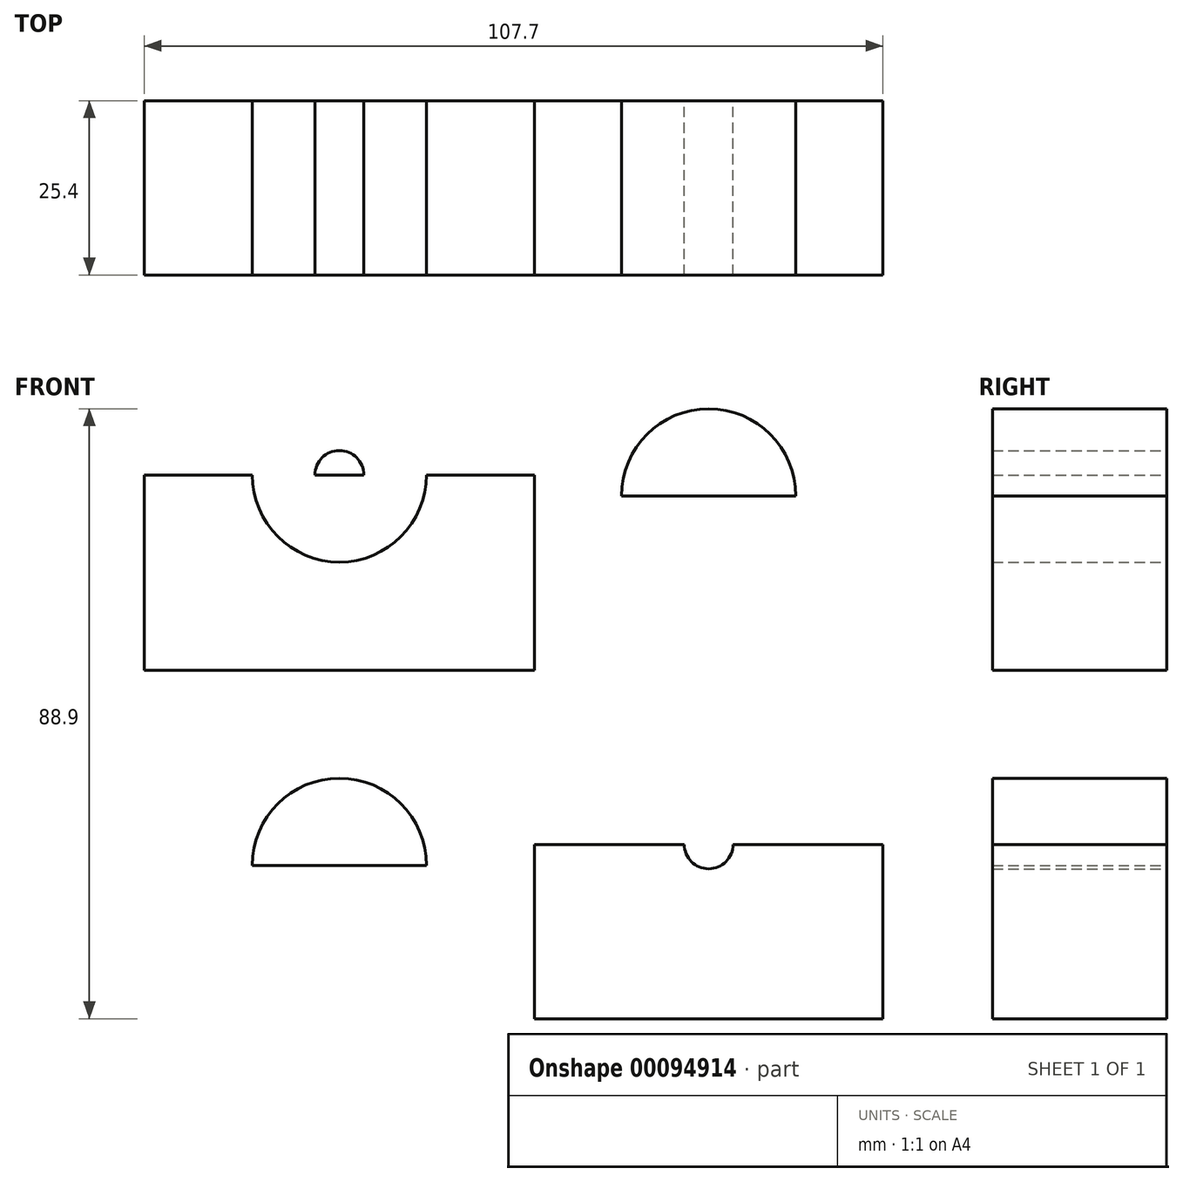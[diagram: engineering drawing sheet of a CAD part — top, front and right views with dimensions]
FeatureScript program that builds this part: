
annotation { "Feature Type Name" : "Feature", "Feature Type Description" : "" }
export const myFeature = defineFeature(function(context is Context, id is Id, definition is map)
    precondition{}
    {
        {
            var Q0;
            Q0=qCreatedBy(makeId("Front.planeOp"),FACE);
            var sketch = newSketch(context, id + "F0", { "sketchPlane" : qUnion([Q0])});
            skLineSegment(sketch, "E0", {"start": v(0, 0) * mm, "end": v(50.8, 0) * mm});
            skLineSegment(sketch, "E1", {"start": v(50.8, 0) * mm, "end": v(50.8, 50.8) * mm});
            skLineSegment(sketch, "E2", {"start": v(50.8, 50.8) * mm, "end": v(0, 50.8) * mm});
            skLineSegment(sketch, "E3", {"start": v(0, 50.8) * mm, "end": v(0, 0) * mm});
            skLineSegment(sketch, "E4", {"start": v(25.4, 50.8) * mm, "end": v(25.4, 0) * mm});
            skLineSegment(sketch, "E5", {"start": v(0, 25.4) * mm, "end": v(50.8, 25.4) * mm});
            skCircle(sketch, "E6", {"center": v(25.4, 25.4) * mm, "radius": 12.7 * mm});
            skCircle(sketch, "E7", {"center": v(25.4, 25.4) * mm, "radius": 3.56 * mm});
            skSolve(sketch);
        }
        {
            var Q0;
            {var subQ0=sQuery(id+"F0.wireOp",EDGE,"E6");var subQ1=sQuery(id+"F0.wireOp",EDGE,"E4");var subQ2=makeQuery(id+"F0.imprint","INTERSECT",VERTEX,{"disambiguationData":[OD(0.0)],"derivedFrom":[subQ1,subQ0]});Q0=makeQuery(id+"F0.imprint","IMPRINT",FACE,{"disambiguationData":[TD([[makeQuery(id+"F0.imprint","IMPRINT",EDGE,{"disambiguationData":[TD([[subQ2,-1.0]])],"derivedFrom":subQ1}),1.0]])]});}
            var Q1;
            {var subQ0=sQuery(id+"F0.wireOp",EDGE,"E6");var subQ1=sQuery(id+"F0.wireOp",EDGE,"E4");var subQ2=makeQuery(id+"F0.imprint","INTERSECT",VERTEX,{"disambiguationData":[OD(0.0)],"derivedFrom":[subQ1,subQ0]});Q1=makeQuery(id+"F0.imprint","IMPRINT",FACE,{"disambiguationData":[TD([[makeQuery(id+"F0.imprint","IMPRINT",EDGE,{"disambiguationData":[TD([[subQ2,-1.0]])],"derivedFrom":subQ1}),-1.0]])]});}
            var Q2;
            {var subQ0=sQuery(id+"F0.wireOp",EDGE,"E7");var subQ1=sQuery(id+"F0.wireOp",EDGE,"E4");var subQ2=makeQuery(id+"F0.imprint","INTERSECT",VERTEX,{"disambiguationData":[OD(1.0)],"derivedFrom":[subQ1,subQ0]});Q2=makeQuery(id+"F0.imprint","IMPRINT",FACE,{"disambiguationData":[TD([[makeQuery(id+"F0.imprint","IMPRINT",EDGE,{"disambiguationData":[TD([[subQ2,-1.0]])],"derivedFrom":subQ1}),-1.0]])]});}
            var Q3;
            {var subQ0=sQuery(id+"F0.wireOp",EDGE,"E7");var subQ1=sQuery(id+"F0.wireOp",EDGE,"E4");var subQ2=makeQuery(id+"F0.imprint","INTERSECT",VERTEX,{"disambiguationData":[OD(1.0)],"derivedFrom":[subQ1,subQ0]});Q3=makeQuery(id+"F0.imprint","IMPRINT",FACE,{"disambiguationData":[TD([[makeQuery(id+"F0.imprint","IMPRINT",EDGE,{"disambiguationData":[TD([[subQ2,-1.0]])],"derivedFrom":subQ1}),1.0]])]});}
            extrude(context, id + "F1", {"entities" : qUnion([Q0, Q1, Q2, Q3]), "depth" : 25.4 * mm});
        }
        {
            var Q0;
            Q0=qCreatedBy(makeId("Front.planeOp"),FACE);
            var sketch = newSketch(context, id + "F2", { "sketchPlane" : qUnion([Q0])});
            skLineSegment(sketch, "E8", {"start": v(0, 0) * mm, "end": v(50.8, 0) * mm});
            skLineSegment(sketch, "E9", {"start": v(50.8, 0) * mm, "end": v(50.8, -50.8) * mm});
            skLineSegment(sketch, "E10", {"start": v(50.8, -50.8) * mm, "end": v(0, -50.8) * mm});
            skLineSegment(sketch, "E11", {"start": v(0, -50.8) * mm, "end": v(0, 0) * mm});
            skLineSegment(sketch, "E12", {"start": v(25.4, 0) * mm, "end": v(25.4, -50.8) * mm});
            skLineSegment(sketch, "E13", {"start": v(50.8, -25.4) * mm, "end": v(0, -25.4) * mm});
            skCircle(sketch, "E14", {"center": v(25.4, -25.4) * mm, "radius": 12.7 * mm});
            skCircle(sketch, "E15", {"center": v(25.4, -25.4) * mm, "radius": 3.56 * mm});
            skSolve(sketch);
        }
        {
            var Q0;
            {var subQ0=sQuery(id+"F2.wireOp",EDGE,"E15");var subQ1=sQuery(id+"F2.wireOp",EDGE,"E12");var subQ2=makeQuery(id+"F2.imprint","INTERSECT",VERTEX,{"disambiguationData":[OD(1.0)],"derivedFrom":[subQ1,subQ0]});Q0=makeQuery(id+"F2.imprint","IMPRINT",FACE,{"disambiguationData":[TD([[makeQuery(id+"F2.imprint","IMPRINT",EDGE,{"disambiguationData":[TD([[subQ2,-1.0]])],"derivedFrom":subQ1}),1.0]])]});}
            var Q1;
            {var subQ0=sQuery(id+"F2.wireOp",EDGE,"E15");var subQ1=sQuery(id+"F2.wireOp",EDGE,"E12");var subQ2=makeQuery(id+"F2.imprint","INTERSECT",VERTEX,{"disambiguationData":[OD(1.0)],"derivedFrom":[subQ1,subQ0]});Q1=makeQuery(id+"F2.imprint","IMPRINT",FACE,{"disambiguationData":[TD([[makeQuery(id+"F2.imprint","IMPRINT",EDGE,{"disambiguationData":[TD([[subQ2,-1.0]])],"derivedFrom":subQ1}),-1.0]])]});}
            var Q2;
            {var subQ0=sQuery(id+"F2.wireOp",EDGE,"E14");var subQ1=sQuery(id+"F2.wireOp",EDGE,"E12");var subQ2=makeQuery(id+"F2.imprint","INTERSECT",VERTEX,{"disambiguationData":[OD(0.0)],"derivedFrom":[subQ1,subQ0]});Q2=makeQuery(id+"F2.imprint","IMPRINT",FACE,{"disambiguationData":[TD([[makeQuery(id+"F2.imprint","IMPRINT",EDGE,{"disambiguationData":[TD([[subQ2,-1.0]])],"derivedFrom":subQ1}),-1.0]])]});}
            var Q3;
            {var subQ0=sQuery(id+"F2.wireOp",EDGE,"E14");var subQ1=sQuery(id+"F2.wireOp",EDGE,"E12");var subQ2=makeQuery(id+"F2.imprint","INTERSECT",VERTEX,{"disambiguationData":[OD(0.0)],"derivedFrom":[subQ1,subQ0]});Q3=makeQuery(id+"F2.imprint","IMPRINT",FACE,{"disambiguationData":[TD([[makeQuery(id+"F2.imprint","IMPRINT",EDGE,{"disambiguationData":[TD([[subQ2,-1.0]])],"derivedFrom":subQ1}),1.0]])]});}
            extrude(context, id + "F3", {"entities" : qUnion([Q0, Q1, Q2, Q3]), "depth" : 25.4 * mm});
        }
        {
            var Q0;
            Q0=qCreatedBy(makeId("Front.planeOp"),FACE);
            var sketch = newSketch(context, id + "F4", { "sketchPlane" : qUnion([Q0])});
            skLineSegment(sketch, "E16", {"start": v(0, 0) * mm, "end": v(-56.9, 0) * mm});
            skLineSegment(sketch, "E17", {"start": v(-56.9, 0) * mm, "end": v(-56.9, 56.9) * mm});
            skLineSegment(sketch, "E18", {"start": v(-56.9, 56.9) * mm, "end": v(0, 56.9) * mm});
            skLineSegment(sketch, "E19", {"start": v(0, 56.9) * mm, "end": v(0, 0) * mm});
            skLineSegment(sketch, "E20", {"start": v(-28.45, 56.9) * mm, "end": v(-28.45, 0) * mm});
            skLineSegment(sketch, "E21", {"start": v(-56.9, 28.45) * mm, "end": v(0, 28.45) * mm});
            skCircle(sketch, "E22", {"center": v(-28.45, 28.45) * mm, "radius": 12.7 * mm});
            skCircle(sketch, "E23", {"center": v(-28.45, 28.45) * mm, "radius": 3.56 * mm});
            skSolve(sketch);
        }
        {
            var Q0;
            {var subQ0=sQuery(id+"F4.wireOp",EDGE,"E22");var subQ1=sQuery(id+"F4.wireOp",EDGE,"E20");var subQ2=makeQuery(id+"F4.imprint","INTERSECT",VERTEX,{"disambiguationData":[OD(0.0)],"derivedFrom":[subQ1,subQ0]});Q0=makeQuery(id+"F4.imprint","IMPRINT",FACE,{"disambiguationData":[TD([[makeQuery(id+"F4.imprint","IMPRINT",EDGE,{"disambiguationData":[TD([[subQ2,-1.0]])],"derivedFrom":subQ1}),-1.0]])]});}
            var Q1;
            {var subQ0=sQuery(id+"F4.wireOp",EDGE,"E22");var subQ1=sQuery(id+"F4.wireOp",EDGE,"E20");var subQ2=makeQuery(id+"F4.imprint","INTERSECT",VERTEX,{"disambiguationData":[OD(0.0)],"derivedFrom":[subQ1,subQ0]});Q1=makeQuery(id+"F4.imprint","IMPRINT",FACE,{"disambiguationData":[TD([[makeQuery(id+"F4.imprint","IMPRINT",EDGE,{"disambiguationData":[TD([[subQ2,-1.0]])],"derivedFrom":subQ1}),1.0]])]});}
            var Q2;
            {var subQ0=sQuery(id+"F4.wireOp",EDGE,"E23");var subQ1=sQuery(id+"F4.wireOp",EDGE,"E20");var subQ2=makeQuery(id+"F4.imprint","INTERSECT",VERTEX,{"disambiguationData":[OD(1.0)],"derivedFrom":[subQ1,subQ0]});Q2=makeQuery(id+"F4.imprint","IMPRINT",FACE,{"disambiguationData":[TD([[makeQuery(id+"F4.imprint","IMPRINT",EDGE,{"disambiguationData":[TD([[subQ2,-1.0]])],"derivedFrom":subQ1}),1.0]])]});}
            var Q3;
            {var subQ0=sQuery(id+"F4.wireOp",EDGE,"E23");var subQ1=sQuery(id+"F4.wireOp",EDGE,"E20");var subQ2=makeQuery(id+"F4.imprint","INTERSECT",VERTEX,{"disambiguationData":[OD(1.0)],"derivedFrom":[subQ1,subQ0]});Q3=makeQuery(id+"F4.imprint","IMPRINT",FACE,{"disambiguationData":[TD([[makeQuery(id+"F4.imprint","IMPRINT",EDGE,{"disambiguationData":[TD([[subQ2,-1.0]])],"derivedFrom":subQ1}),-1.0]])]});}
            var Q4;
            Q4 = qSketchRegion(id + "F6", true);
            extrude(context, id + "F5", {"entities" : qUnion([Q0, Q1, Q2, Q3, Q4]), "depth" : 25.4 * mm});
        }
        {
            var Q0;
            Q0=qCreatedBy(makeId("Front.planeOp"),FACE);
            var sketch = newSketch(context, id + "F6", { "sketchPlane" : qUnion([Q0])});
            skLineSegment(sketch, "E24", {"start": v(0, 0) * mm, "end": v(0, -56.9) * mm});
            skLineSegment(sketch, "E25", {"start": v(0, -56.9) * mm, "end": v(-56.9, -56.9) * mm});
            skLineSegment(sketch, "E26", {"start": v(-56.9, -56.9) * mm, "end": v(-56.9, 0) * mm});
            skLineSegment(sketch, "E27", {"start": v(-56.9, 0) * mm, "end": v(0, 0) * mm});
            skLineSegment(sketch, "E28", {"start": v(-28.45, 0) * mm, "end": v(-28.45, -56.9) * mm});
            skLineSegment(sketch, "E29", {"start": v(-56.9, -28.45) * mm, "end": v(0, -28.45) * mm});
            skCircle(sketch, "E30", {"center": v(-28.45, -28.45) * mm, "radius": 12.7 * mm});
            skCircle(sketch, "E31", {"center": v(-28.45, -28.45) * mm, "radius": 3.56 * mm});
            skSolve(sketch);
        }
        {
            var Q0;
            {var subQ0=sQuery(id+"F6.wireOp",EDGE,"E30");var subQ1=sQuery(id+"F6.wireOp",EDGE,"E28");var subQ2=makeQuery(id+"F6.imprint","INTERSECT",VERTEX,{"disambiguationData":[OD(0.0)],"derivedFrom":[subQ1,subQ0]});Q0=makeQuery(id+"F6.imprint","IMPRINT",FACE,{"disambiguationData":[TD([[makeQuery(id+"F6.imprint","IMPRINT",EDGE,{"disambiguationData":[TD([[subQ2,-1.0]])],"derivedFrom":subQ1}),-1.0]])]});}
            var Q1;
            {var subQ0=sQuery(id+"F6.wireOp",EDGE,"E30");var subQ1=sQuery(id+"F6.wireOp",EDGE,"E28");var subQ2=makeQuery(id+"F6.imprint","INTERSECT",VERTEX,{"disambiguationData":[OD(0.0)],"derivedFrom":[subQ1,subQ0]});Q1=makeQuery(id+"F6.imprint","IMPRINT",FACE,{"disambiguationData":[TD([[makeQuery(id+"F6.imprint","IMPRINT",EDGE,{"disambiguationData":[TD([[subQ2,-1.0]])],"derivedFrom":subQ1}),1.0]])]});}
            var Q2;
            {var subQ0=sQuery(id+"F6.wireOp",EDGE,"E31");var subQ1=sQuery(id+"F6.wireOp",EDGE,"E28");var subQ2=makeQuery(id+"F6.imprint","INTERSECT",VERTEX,{"disambiguationData":[OD(1.0)],"derivedFrom":[subQ1,subQ0]});Q2=makeQuery(id+"F6.imprint","IMPRINT",FACE,{"disambiguationData":[TD([[makeQuery(id+"F6.imprint","IMPRINT",EDGE,{"disambiguationData":[TD([[subQ2,-1.0]])],"derivedFrom":subQ1}),1.0]])]});}
            var Q3;
            {var subQ0=sQuery(id+"F6.wireOp",EDGE,"E31");var subQ1=sQuery(id+"F6.wireOp",EDGE,"E28");var subQ2=makeQuery(id+"F6.imprint","INTERSECT",VERTEX,{"disambiguationData":[OD(1.0)],"derivedFrom":[subQ1,subQ0]});Q3=makeQuery(id+"F6.imprint","IMPRINT",FACE,{"disambiguationData":[TD([[makeQuery(id+"F6.imprint","IMPRINT",EDGE,{"disambiguationData":[TD([[subQ2,-1.0]])],"derivedFrom":subQ1}),-1.0]])]});}
            extrude(context, id + "F7", {"entities" : qUnion([Q0, Q1, Q2, Q3]), "depth" : 25.4 * mm});
        }
    });
